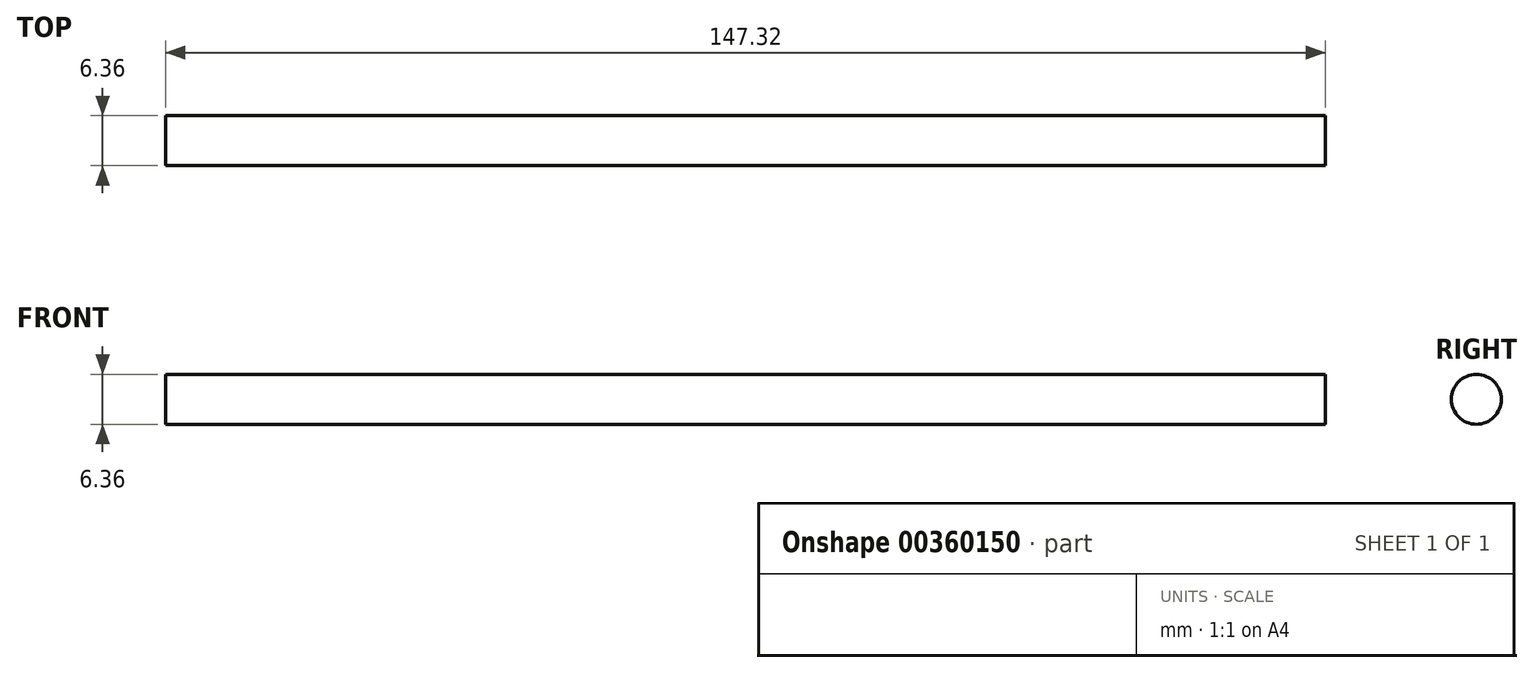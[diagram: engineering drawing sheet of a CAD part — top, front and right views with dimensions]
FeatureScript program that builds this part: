
annotation { "Feature Type Name" : "Feature", "Feature Type Description" : "" }
export const myFeature = defineFeature(function(context is Context, id is Id, definition is map)
    precondition{}
    {
        {
            var Q0;
            Q0=qCreatedBy(makeId("Front.planeOp"),FACE);
            var sketch = newSketch(context, id + "F0", { "sketchPlane" : qUnion([Q0])});
            skLineSegment(sketch, "E0", {"start": v(-73.66, 0) * mm, "end": v(-73.66, 3.18) * mm});
            skLineSegment(sketch, "E1", {"start": v(-73.66, 3.18) * mm, "end": v(73.66, 3.18) * mm});
            skLineSegment(sketch, "E2", {"start": v(73.66, 3.18) * mm, "end": v(73.66, 0) * mm});
            skLineSegment(sketch, "E3", {"start": v(73.66, 0) * mm, "end": v(-73.66, 0) * mm});
            skSolve(sketch);
        }
        {
            var Q0;
            Q0=makeQuery(id+"F0.imprint","IMPRINT",FACE,{"disambiguationData":[TD([[makeQuery(id+"F0.imprint","IMPRINT",EDGE,{"derivedFrom":sQuery(id+"F0.wireOp",EDGE,"E0")}),-1.0]])]});
            var Q1;
            Q1=sQuery(id+"F0.wireOp",EDGE,"E3");
            revolve(context, id + "F1", {"entities" : qUnion([Q0]), "axis" : qUnion([Q1]), "revolveType" : RevolveType.FULL});
        }
    });
